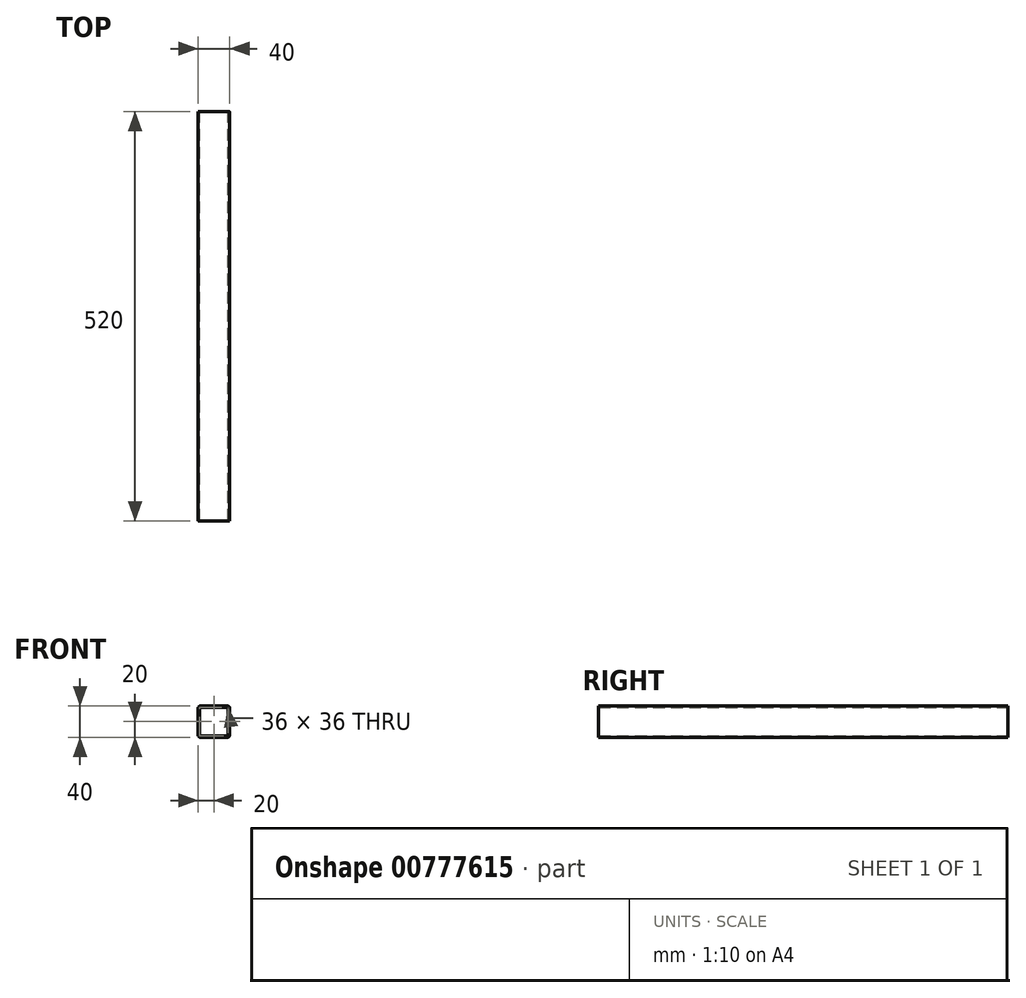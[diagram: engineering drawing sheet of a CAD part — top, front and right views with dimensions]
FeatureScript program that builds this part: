
annotation { "Feature Type Name" : "Feature", "Feature Type Description" : "" }
export const myFeature = defineFeature(function(context is Context, id is Id, definition is map)
    precondition{}
    {
        {
            var Q0;
            Q0=qCreatedBy(makeId("Front.planeOp"),FACE);
            var sketch = newSketch(context, id + "F0", { "sketchPlane" : qUnion([Q0])});
            skLineSegment(sketch, "E0.bottom", {"start": v(17, 20) * mm, "end": v(-17, 20) * mm});
            skLineSegment(sketch, "E0.top", {"start": v(17, -20) * mm, "end": v(-17, -20) * mm});
            skLineSegment(sketch, "E0.left", {"start": v(20, 17) * mm, "end": v(20, -17) * mm});
            skLineSegment(sketch, "E0.right", {"start": v(-20, 17) * mm, "end": v(-20, -17) * mm});
            skPoint(sketch, "E0.middle", {"position": v(0, 0) * mm});
            skPoint(sketch, "E1.visualSharp", {"position": v(-20, 20) * mm});
            skArc(sketch, "E1.filletArc", {"start": v(-17, 20) * mm, "mid": v(-19.12, 19.12) * mm, "end": v(-20, 17) * mm});
            skPoint(sketch, "E2.visualSharp", {"position": v(20, 20) * mm});
            skArc(sketch, "E2.filletArc", {"start": v(20, 17) * mm, "mid": v(19.12, 19.12) * mm, "end": v(17, 20) * mm});
            skPoint(sketch, "E3.visualSharp", {"position": v(20, -20) * mm});
            skArc(sketch, "E3.filletArc", {"start": v(17, -20) * mm, "mid": v(19.12, -19.12) * mm, "end": v(20, -17) * mm});
            skPoint(sketch, "E4.visualSharp", {"position": v(-20, -20) * mm});
            skArc(sketch, "E4.filletArc", {"start": v(-20, -17) * mm, "mid": v(-19.12, -19.12) * mm, "end": v(-17, -20) * mm});
            skLineSegment(sketch, "E5.0", {"start": v(18, 18) * mm, "end": v(-18, 18) * mm});
            skLineSegment(sketch, "E5.1", {"start": v(18, 18) * mm, "end": v(18, -18) * mm});
            skLineSegment(sketch, "E5.2", {"start": v(18, -18) * mm, "end": v(-18, -18) * mm});
            skLineSegment(sketch, "E5.3", {"start": v(-18, 18) * mm, "end": v(-18, -18) * mm});
            skSolve(sketch);
        }
        {
            var Q0;
            Q0=makeQuery(id+"F0.imprint","IMPRINT",FACE,{"disambiguationData":[TD([[makeQuery(id+"F0.imprint","IMPRINT",EDGE,{"derivedFrom":sQuery(id+"F0.wireOp",EDGE,"E0.bottom")}),1.0]])]});
            extrude(context, id + "F1", {"entities" : qUnion([Q0]), "endBound" : BoundingType.SYMMETRIC, "depth" : 520 * mm, "offsetDistance" : 25 * mm});
        }
    });
